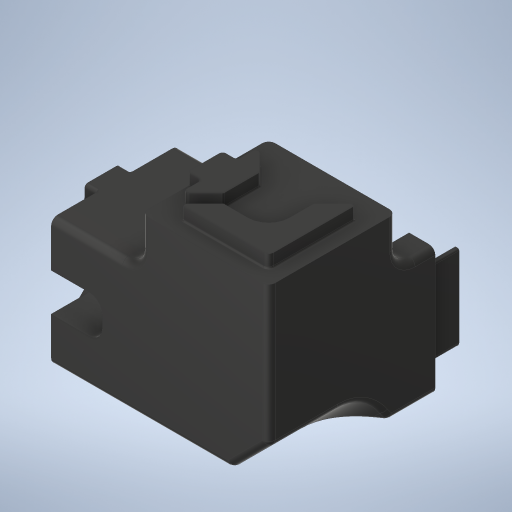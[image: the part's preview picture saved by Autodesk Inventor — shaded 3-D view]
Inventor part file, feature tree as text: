
AUTODESK INVENTOR PART (.ipt)
format: ipt  version: 2024 (Build 280153000, 153)  size: 1,004,032 bytes
history: native  units: mm
features: extrude x17, sketch x15, fillet x14, projected_geometry x13, plane x7, other x4, reference x2, hole x1
ambient origin geometry x8: Origin, YZ Plane, XZ Plane, XY Plane, X Axis, Y Axis, Z Axis, Center Point
bodies: Solid2 (feature_tree)
feature tree (73):
  extrude  "Extrusion2"  Depth=6.0mm TaperAngle=0.0deg
  extrude  "Extrusion3"  Depth=1.0mm
  sketch  "Sketch4"  dims[d18=0.0mm d19=0.0mm d21=1.0mm]
  extrude  "Extrusion4"  Depth=20.0mm
  plane  "Work Plane4"
  extrude  "Extrusion5"  Depth=0.25mm
  plane  "Work Plane5"
  extrude  "Extrusion6"  [1 undecoded]
  plane  "Work Plane6"
  extrude  "Extrusion7"  Depth=7.8mm
  extrude  "Extrusion8"  Depth=20.0mm
  plane  "Work Plane7"
  extrude  "Extrusion9"  Depth=14.15mm
  fillet  "Fillet1"  Radius=20.0mm
  extrude  "Extrusion10"  Depth=24.35mm TaperAngle=0.0deg
  fillet  "Fillet2"  Radius=6.0mm
  fillet  "Fillet3"  Radius=6.0mm
  fillet  "Fillet4"  Radius=15.0mm
  fillet  "Fillet5"  [1 undecoded]
  sketch  "Sketch10"  dims[d34=18.0mm d35=0.0mm d36=14.15mm d37=20.0mm]
  sketch  "Sketch11"  dims[d38=20.0mm d39=24.35mm d40=0.0mm d41=6.0mm d42=6.0mm d43=15.0mm d44=0.0mm d45=45.0deg]
  extrude  "Extrusion12"  Depth=10.0mm
  extrude  "Extrusion11"  Depth=3.0mm
  fillet  "Fillet6"  Radius=1.0mm
  extrude  "Extrusion13"  Depth=1.0mm
  fillet  "Fillet7"  Radius=8.0mm
  extrude  "Extrusion14"  Depth=2.0mm TaperAngle=0.0deg
  extrude  "Extrusion15"  Depth=2.0mm TaperAngle=0.0deg
  fillet  "Fillet8"  Radius=0.5mm
  fillet  "Fillet9"  Radius=2.0mm
  extrude  "Extrusion16"  Depth=2.0mm TaperAngle=0.0deg
  fillet  "Fillet10"  Radius=0.5mm
  sketch  "Sketch16"  dims[d61=0.25mm d62=2.0mm d63=0.0mm d64=0.5mm d65=2.0mm d66=0.0mm]
  plane  "Work Plane10"
  extrude  "Extrusion17"  Depth=0.5mm
  extrude  "Extrusion18"  Depth=10.5mm
  hole  "Hole2"  [1 undecoded]
  fillet  "Fillet11"  Radius=0.5mm
  fillet  "Fillet12"  Radius=8.25mm
  fillet  "Fillet13"  Radius=18.0mm
  fillet  "Fillet14"  Radius=11.5mm
  sketch  "Sketch_64"  dims[d69=0.25mm d70=2.0mm d71=0.0mm d72=0.5mm d73=0.5mm d74=10.5mm d75=6.0mm d76=0.0mm d77=0.5mm d78=8.25mm d79=18.0mm d80=11.5mm d81=-3.0mm d82=-2.0mm d83=-6.0mm d84=2.0mm d85=0.0mm d86=10.0mm d87=0.0mm d88=5.2mm d89=6.0mm d90=4.0mm d91=2.0mm d92=90.0deg d93=8.0mm d94=0.0mm d95=0.5mm d96=0.5mm d97=0.25mm d98=0.25mm d99=0.25mm d100=0.25mm d60=0.0mm]
  sketch  "Sketch3"  dims[d14=11.3mm d15=6.0mm d16=0.0mm]
  projected_geometry  "Projected Loop1"
  projected_geometry  "Projected Loop2"
  sketch  "Sketch5"  dims[d22=20.0mm d23=20.0mm]
  sketch  "Sketch6"  dims[d24=1.0mm d25=0.25mm]
  projected_geometry  "Projected Loop3"
  sketch  "Sketch7"  dims[d26=6.15mm d27=0.0mm d28=-26.15mm]
  projected_geometry  "Projected Loop4"
  sketch  "Sketch8"  dims[d29=6.55mm d30=0.0mm d31=7.8mm]
  projected_geometry  "Projected Loop5"
  sketch  "Sketch9"  dims[d32=20.0mm d33=20.0mm]
  projected_geometry  "Projected Loop6"
  reference  "Reference1"
  reference  "Reference2"
  sketch  "Sketch12"  dims[d46=12.0mm d47=0.0mm d48=10.0mm]
  projected_geometry  "Projected Loop7"
  sketch  "Sketch13"  dims[d49=10.0mm d50=0.0mm d51=3.0mm d52=1.0mm]
  projected_geometry  "Projected Loop8"
  projected_geometry  "Projected Loop9"
  sketch  "Sketch14"  dims[d53=3.0mm d54=1.0mm d55=8.0mm d56=0.0mm]
  projected_geometry  "Projected Loop10"
  projected_geometry  "Projected Loop12"
  sketch  "Sketch15"  dims[d57=2.0mm d58=2.0mm d59=0.0mm]
  projected_geometry  "Projected Loop13"
  projected_geometry  "Projected Loop14"
  plane  "Work Plane8"
  plane  "Work Plane9"
  parser-record x1  (decoder bookkeeping rows leaked as tree rows — omitted from the tree; the rows remain in map.json)
  other  "Printer Frame Assembly RevI.iam"
  other  "HFSFB5-2020-440:2"
  other  "HFSTB5-2020-650:4"
note: 3 required parameter values undecoded (feature->parameter linkage not recoverable at this tier; creation-order binding heuristic only, values carry confidence <= 0.55)
note: 1 file-system path scrubbed to <path> (originals preserved in map.json)
